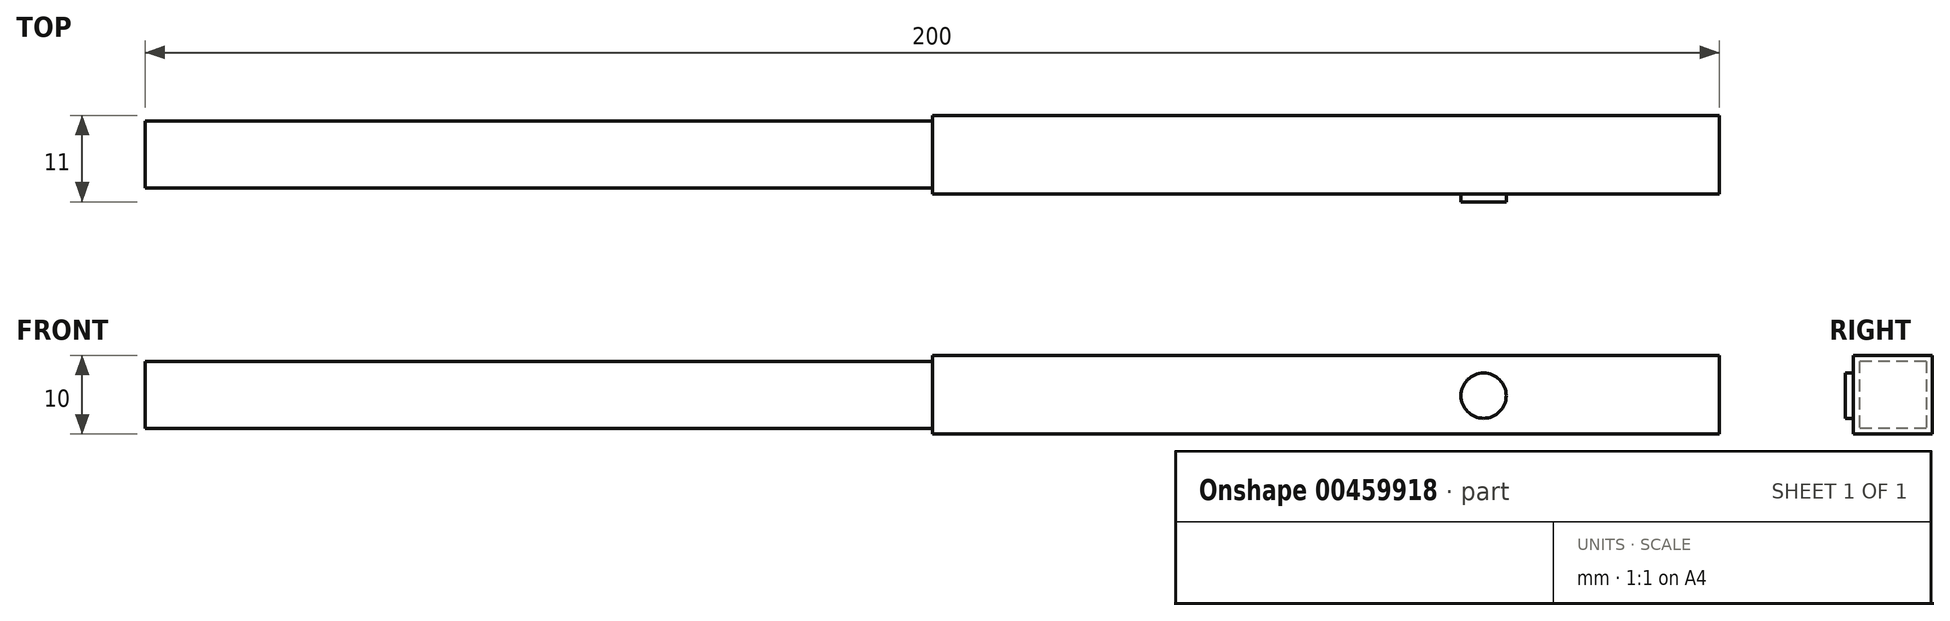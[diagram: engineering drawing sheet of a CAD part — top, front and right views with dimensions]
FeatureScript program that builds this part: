
annotation { "Feature Type Name" : "Feature", "Feature Type Description" : "" }
export const myFeature = defineFeature(function(context is Context, id is Id, definition is map)
    precondition{}
    {
        {
            var Q0;
            Q0=qCreatedBy(makeId("Front.planeOp"),FACE);
            var sketch = newSketch(context, id + "F0", { "sketchPlane" : qUnion([Q0])});
            skLineSegment(sketch, "E0.bottom", {"start": v(-50.95, -7.72) * mm, "end": v(49.05, -7.72) * mm});
            skLineSegment(sketch, "E0.top", {"start": v(-50.95, 2.28) * mm, "end": v(49.05, 2.28) * mm});
            skLineSegment(sketch, "E0.left", {"start": v(-50.95, -7.72) * mm, "end": v(-50.95, 2.28) * mm});
            skLineSegment(sketch, "E0.right", {"start": v(49.05, -7.72) * mm, "end": v(49.05, 2.28) * mm});
            skSolve(sketch);
        }
        {
            var Q0;
            Q0=makeQuery(id+"F0.imprint","IMPRINT",FACE,{"disambiguationData":[TD([[makeQuery(id+"F0.imprint","IMPRINT",EDGE,{"derivedFrom":sQuery(id+"F0.wireOp",EDGE,"E0.bottom")}),1.0]])]});
            extrude(context, id + "F1", {"entities" : qUnion([Q0]), "depth" : 10 * mm});
        }
        {
            var Q0;
            Q0=makeQuery(id+"F1.opExtrude","SWEPT_FACE",FACE,{"disambiguationData":[OSD([sQuery(id+"F0.wireOp",EDGE,"E0.left")])]});
            var sketch = newSketch(context, id + "F2", { "sketchPlane" : qUnion([Q0])});
            skLineSegment(sketch, "E1.bottom", {"start": v(0.75, 1.53) * mm, "end": v(9.25, 1.53) * mm});
            skLineSegment(sketch, "E1.top", {"start": v(0.75, -6.97) * mm, "end": v(9.25, -6.97) * mm});
            skLineSegment(sketch, "E1.left", {"start": v(0.75, 1.53) * mm, "end": v(0.75, -6.97) * mm});
            skLineSegment(sketch, "E1.right", {"start": v(9.25, 1.53) * mm, "end": v(9.25, -6.97) * mm});
            skSolve(sketch);
        }
        {
            var Q0;
            Q0=makeQuery(id+"F2.imprint","IMPRINT",FACE,{"disambiguationData":[TD([[makeQuery(id+"F2.imprint","IMPRINT",EDGE,{"derivedFrom":sQuery(id+"F2.wireOp",EDGE,"E1.bottom")}),-1.0]])]});
            extrude(context, id + "F3", {"entities" : qUnion([Q0]), "operationType" : NewBodyOperationType.ADD, "depth" : 100 * mm});
        }
        {
            var Q0;
            Q0=makeQuery(id+"F1.opExtrude","CAP_FACE",FACE,{"disambiguationData":[OSD([sQuery(id+"F0.wireOp",EDGE,"E0.bottom"),sQuery(id+"F0.wireOp",EDGE,"E0.top"),sQuery(id+"F0.wireOp",EDGE,"E0.left"),sQuery(id+"F0.wireOp",EDGE,"E0.right")])],"isStart":false});
            var sketch = newSketch(context, id + "F4", { "sketchPlane" : qUnion([Q0])});
            skCircle(sketch, "E2", {"center": v(19.08, -2.83) * mm, "radius": 2.87 * mm});
            skSolve(sketch);
        }
        {
            var Q0;
            Q0=makeQuery(id+"F4.imprint","IMPRINT",FACE,{"disambiguationData":[TD([[makeQuery(id+"F4.imprint","IMPRINT",EDGE,{"derivedFrom":sQuery(id+"F4.wireOp",EDGE,"E2")}),1.0]])]});
            extrude(context, id + "F5", {"entities" : qUnion([Q0]), "operationType" : NewBodyOperationType.ADD, "depth" : 1 * mm});
        }
    });
